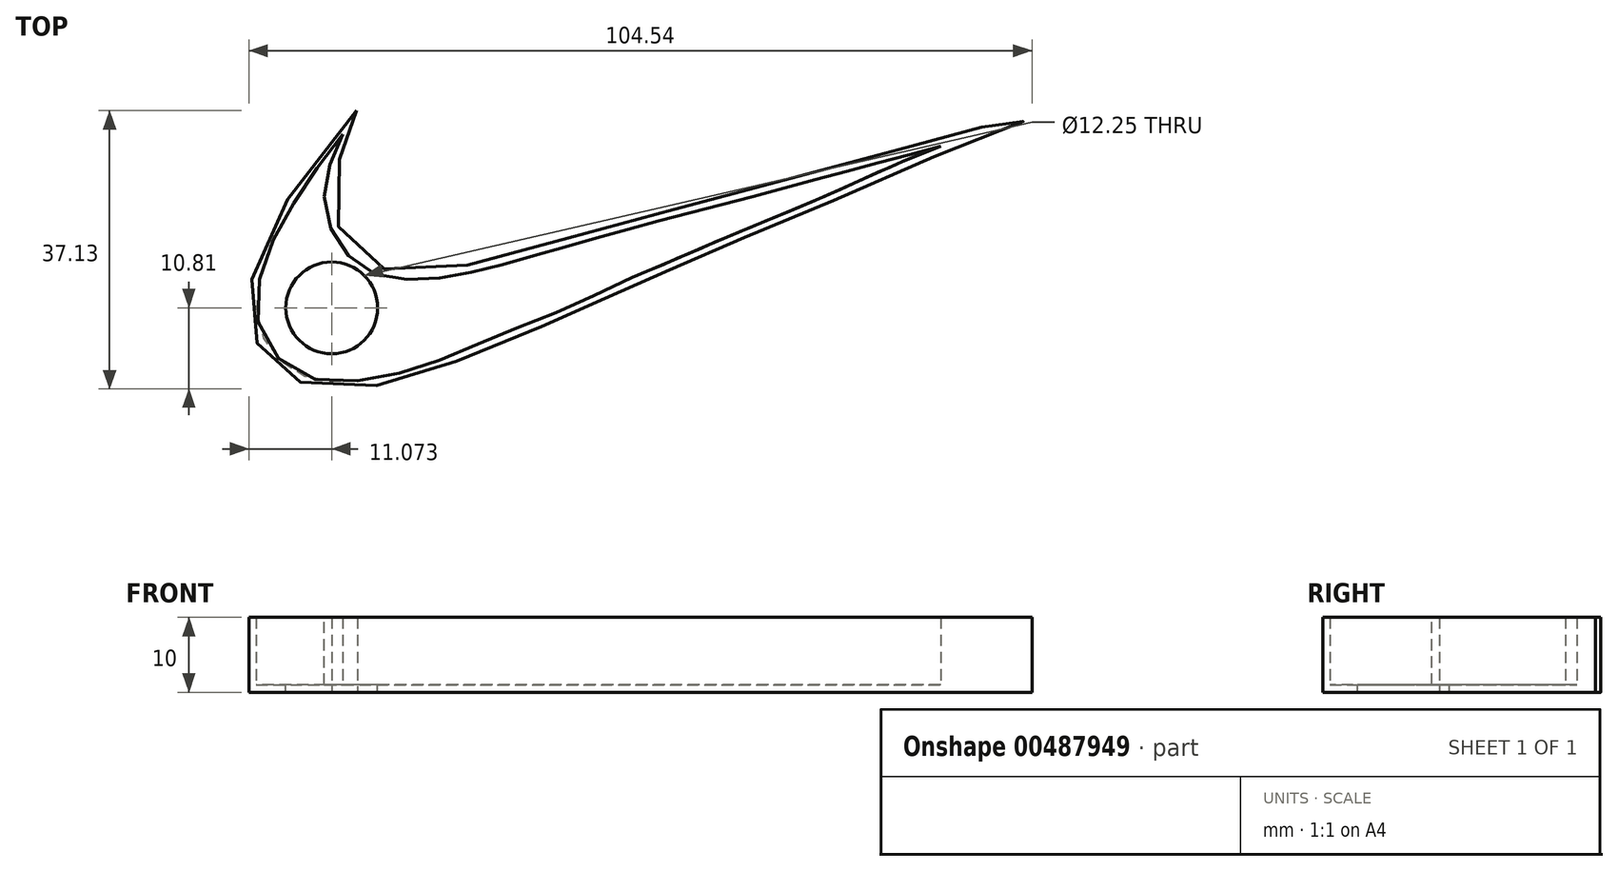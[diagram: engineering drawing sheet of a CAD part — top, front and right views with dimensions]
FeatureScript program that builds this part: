
annotation { "Feature Type Name" : "Feature", "Feature Type Description" : "" }
export const myFeature = defineFeature(function(context is Context, id is Id, definition is map)
    precondition{}
    {
        {
            var Q0;
            Q0=qCreatedBy(makeId("Top.planeOp"),FACE);
            var sketch = newSketch(context, id + "F0", { "sketchPlane" : qUnion([Q0])});
            skFitSpline(sketch, "E0", {"points": [v(-32.1, 23.34) * mm, v(-41.76, 10.84) * mm, v(-45.8, 1.97) * mm, v(-46.49, -2.85) * mm, v(-45.1, -8.17) * mm, v(-42.05, -11.42) * mm, v(-38.5, -13.3) * mm, v(-31.12, -13.59) * mm, v(-22.16, -11.42) * mm, v(-14.67, -8.37) * mm, v(-4.43, -4.23) * mm, v(0, -2.26) * mm, v(4.73, 0) * mm, v(11.03, 2.66) * mm, v(18.52, 5.91) * mm, v(28.24, 9.9) * mm, v(41.82, 15.9) * mm, v(53.45, 20.48) * mm, v(58.04, 22.6) * mm, v(52.22, 21.36) * mm, v(45.7, 19.6) * mm, v(28.6, 15.02) * mm, v(13.96, 11.14) * mm, v(0, 7.43) * mm, v(-13.73, 3.55) * mm, v(-23.96, 1.8) * mm, v(-30.48, 3.03) * mm, v(-33.83, 6.55) * mm, v(-35.42, 11.49) * mm, v(-34.18, 17.3) * mm, v(-32.6, 20.84) * mm, v(-32.1, 23.34) * mm]});
            skCircle(sketch, "E1", {"center": v(-35.42, -2.97) * mm, "radius": 5.13 * mm});
            skSolve(sketch);
        }
        {
            var Q0;
            Q0 = qSketchRegion(id + "F0", true);
            extrude(context, id + "F1", {"entities" : qUnion([Q0]), "depth" : 10 * mm});
        }
        {
            var Q0;
            Q0=makeQuery(id+"F1.opExtrude","CAP_FACE",FACE,{"disambiguationData":[OSD([sQuery(id+"F0.wireOp",EDGE,"E0")])],"isStart":false});
            shell(context, id + "F2", {"entities" : qUnion([Q0]), "thickness" : 1 * mm});
        }
        {
            var Q0;
            {var subQ0=sQuery(id+"F0.wireOp",EDGE,"E1");var subQ1=sQuery(id+"F0.wireOp",EDGE,"E0");Q0=makeQuery(id+"F2.opShell","OFFSET_FACE",FACE,{"disambiguationData":[OSD([subQ1,subQ0]),TDD([makeQuery(id+"F1.opExtrude","CAP_FACE",FACE,{"disambiguationData":[OSD([subQ1,subQ0])],"isStart":false})])]});}
            extrude(context, id + "F3", {"entities" : qUnion([Q0]), "operationType" : NewBodyOperationType.REMOVE, "oppositeDirection" : true, "depth" : 25.4 * mm});
        }
    });
